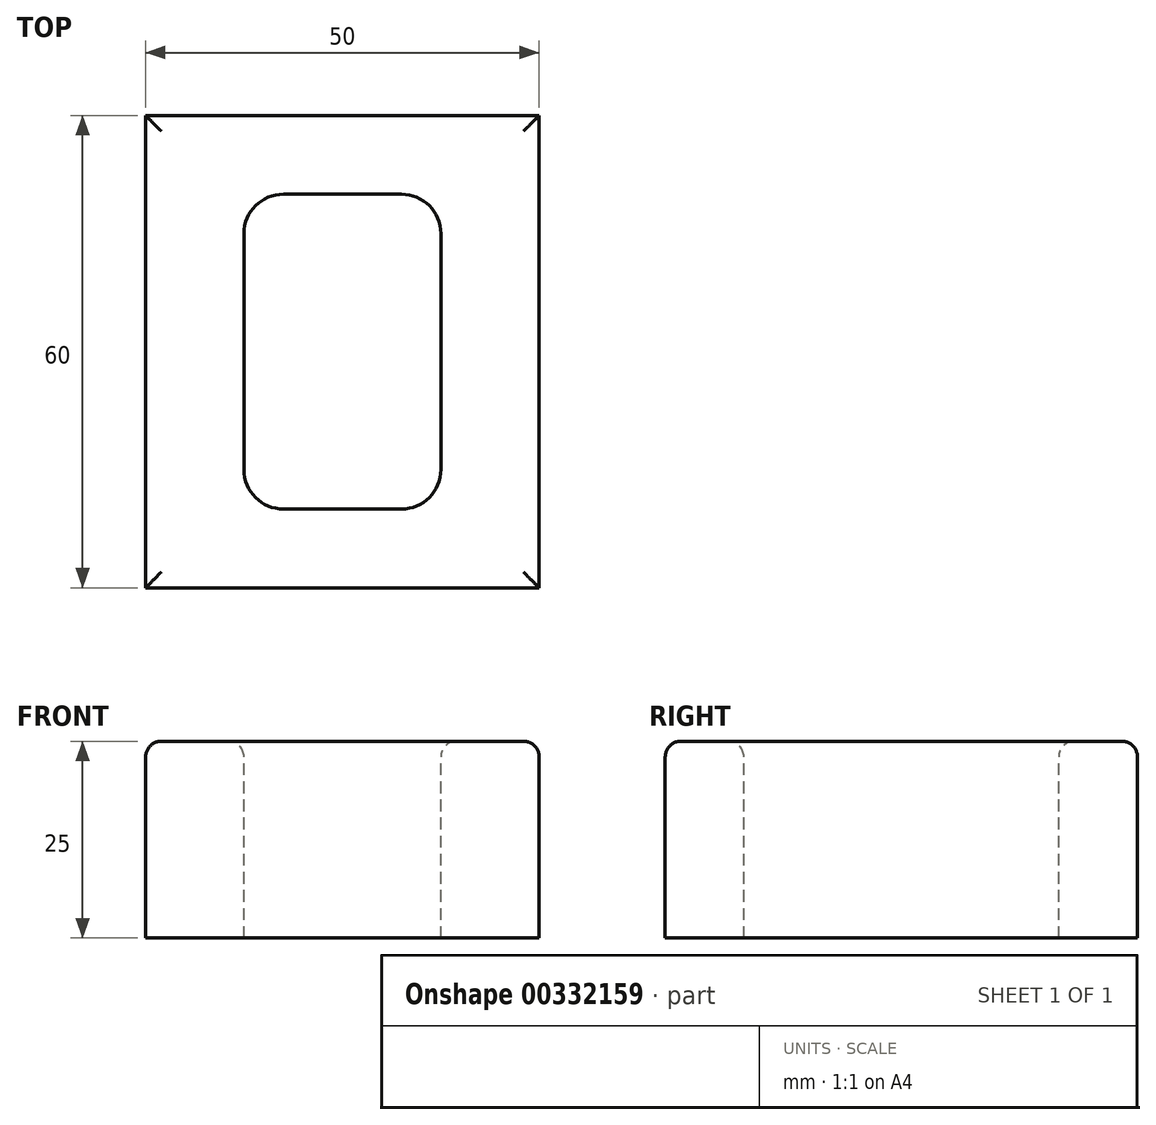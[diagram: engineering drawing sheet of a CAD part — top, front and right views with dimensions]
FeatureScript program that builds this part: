
annotation { "Feature Type Name" : "Feature", "Feature Type Description" : "" }
export const myFeature = defineFeature(function(context is Context, id is Id, definition is map)
    precondition{}
    {
        {
            var Q0;
            Q0=qCreatedBy(makeId("Top.planeOp"),FACE);
            var sketch = newSketch(context, id + "F0", { "sketchPlane" : qUnion([Q0])});
            skLineSegment(sketch, "E0.bottom", {"start": v(25, 30) * mm, "end": v(-25, 30) * mm});
            skLineSegment(sketch, "E0.top", {"start": v(25, -30) * mm, "end": v(-25, -30) * mm});
            skLineSegment(sketch, "E0.left", {"start": v(25, 30) * mm, "end": v(25, -30) * mm});
            skLineSegment(sketch, "E0.right", {"start": v(-25, 30) * mm, "end": v(-25, -30) * mm});
            skPoint(sketch, "E0.middle", {"position": v(0, 0) * mm});
            skSolve(sketch);
        }
        {
            var Q0;
            Q0 = qSketchRegion(id + "F0", true);
            extrude(context, id + "F1", {"entities" : qUnion([Q0]), "endBound" : BoundingType.SYMMETRIC, "depth" : 25 * mm});
        }
        {
            var Q0;
            Q0=makeQuery(id+"F1.opExtrude","CAP_FACE",FACE,{"disambiguationData":[OSD([sQuery(id+"F0.wireOp",EDGE,"E0.bottom"),sQuery(id+"F0.wireOp",EDGE,"E0.top"),sQuery(id+"F0.wireOp",EDGE,"E0.left"),sQuery(id+"F0.wireOp",EDGE,"E0.right")])],"isStart":false});
            var sketch = newSketch(context, id + "F2", { "sketchPlane" : qUnion([Q0])});
            skLineSegment(sketch, "E1.bottom", {"start": v(12.5, -20) * mm, "end": v(-12.5, -20) * mm});
            skLineSegment(sketch, "E1.top", {"start": v(12.5, 20) * mm, "end": v(-12.5, 20) * mm});
            skLineSegment(sketch, "E1.left", {"start": v(12.5, -20) * mm, "end": v(12.5, 20) * mm});
            skLineSegment(sketch, "E1.right", {"start": v(-12.5, -20) * mm, "end": v(-12.5, 20) * mm});
            skPoint(sketch, "E1.middle", {"position": v(0, 0) * mm});
            skSolve(sketch);
        }
        {
            var Q0;
            Q0=makeQuery(id+"F2.imprint","IMPRINT",FACE,{"disambiguationData":[TD([[makeQuery(id+"F2.imprint","IMPRINT",EDGE,{"derivedFrom":sQuery(id+"F2.wireOp",EDGE,"E1.bottom")}),-1.0]])]});
            extrude(context, id + "F3", {"entities" : qUnion([Q0]), "operationType" : NewBodyOperationType.REMOVE, "endBound" : BoundingType.THROUGH_ALL, "oppositeDirection" : true, "depth" : 41.9 * mm});
        }
        {
            var Q0;
            Q0=makeQuery(id+"F3.boolean.opBoolean","COPY",EDGE,{"derivedFrom":makeQuery(id+"F3.opExtrude","SWEPT_EDGE",EDGE,{"disambiguationData":[OSD([sQuery(id+"F2.wireOp",EDGE,"E1.bottom"),sQuery(id+"F2.wireOp",EDGE,"E1.left")])]})});
            var Q1;
            Q1=makeQuery(id+"F3.boolean.opBoolean","COPY",EDGE,{"derivedFrom":makeQuery(id+"F3.opExtrude","SWEPT_EDGE",EDGE,{"disambiguationData":[OSD([sQuery(id+"F2.wireOp",EDGE,"E1.bottom"),sQuery(id+"F2.wireOp",EDGE,"E1.right")])]})});
            var Q2;
            Q2=makeQuery(id+"F3.boolean.opBoolean","COPY",EDGE,{"derivedFrom":makeQuery(id+"F3.opExtrude","SWEPT_EDGE",EDGE,{"disambiguationData":[OSD([sQuery(id+"F2.wireOp",EDGE,"E1.top"),sQuery(id+"F2.wireOp",EDGE,"E1.right")])]})});
            var Q3;
            Q3=makeQuery(id+"F3.boolean.opBoolean","COPY",EDGE,{"derivedFrom":makeQuery(id+"F3.opExtrude","SWEPT_EDGE",EDGE,{"disambiguationData":[OSD([sQuery(id+"F2.wireOp",EDGE,"E1.top"),sQuery(id+"F2.wireOp",EDGE,"E1.left")])]})});
            fillet(context, id + "F4", {"entities" : qUnion([Q0, Q1, Q2, Q3]), "radius" : 5 * mm, "tangentPropagation" : true, "allowEdgeOverflow" : false});
        }
        {
            var Q0;
            Q0=makeQuery(id+"F1.opExtrude","CAP_FACE",FACE,{"disambiguationData":[OSD([sQuery(id+"F0.wireOp",EDGE,"E0.bottom"),sQuery(id+"F0.wireOp",EDGE,"E0.top"),sQuery(id+"F0.wireOp",EDGE,"E0.left"),sQuery(id+"F0.wireOp",EDGE,"E0.right")])],"isStart":false});
            fillet(context, id + "F5", {"entities" : qUnion([Q0]), "radius" : 2 * mm, "tangentPropagation" : true, "allowEdgeOverflow" : false});
        }
    });
